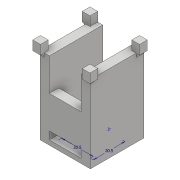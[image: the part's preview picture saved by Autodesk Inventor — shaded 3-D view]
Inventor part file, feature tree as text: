
AUTODESK INVENTOR PART (.ipt)
format: ipt  version: 2018 (Build 220112000, 112)  size: 214,016 bytes
history: native  units: mm
features: extrude x8, sketch x7, fillet x1
ambient origin geometry x8: Origin, YZ Plane, XZ Plane, XY Plane, X Axis, Y Axis, Z Axis, Center Point
bodies: Solid1 (feature_tree)
feature tree (16):
  sketch  "Sketch1"  dims[d0=20.5mm d1=20.5mm]
  extrude  "Extrusion1"  Depth=20.5mm
  extrude  "Extrusion2"  Depth=3.0mm TaperAngle=0.0deg
  extrude  "Extrusion3"  Depth=20.5mm
  extrude  "Extrusion4"  Depth=29.0mm TaperAngle=0.0deg
  extrude  "Extrusion5"  Depth=21.0mm TaperAngle=0.0deg
  extrude  "Extrusion6"  Depth=3.0mm
  extrude  "Extrusion7"  Depth=10.0mm
  extrude  "Extrusion8"  Depth=2.5mm
  fillet  "Fillet1"  Radius=13.5mm
  sketch  "Sketch2"  dims[d2=3.0mm d3=3.0mm d4=0.0mm]
  sketch  "Sketch4"  dims[d5=29.0mm d6=0.0mm d7=20.5mm]
  sketch  "Sketch5"  dims[d8=5.0mm d9=29.0mm d10=0.0mm]
  sketch  "Sketch6"  dims[d11=3.0mm d12=0.0mm d13=21.0mm d14=0.0mm]
  sketch  "Sketch7"  dims[d15=3.0mm d16=3.0mm]
  sketch  "Sketch8"  dims[d17=21.0mm d18=0.0mm d19=10.0mm d20=13.5mm d21=13.5mm d22=27.0mm d23=27.0mm d24=27.0mm d25=5.0mm d26=5.0mm d27=5.0mm d28=5.0mm d29=5.0mm d30=5.0mm d31=5.0mm d32=5.0mm d33=5.0mm d34=0.0mm d35=6.0mm d36=0.0mm d37=2.5mm]
